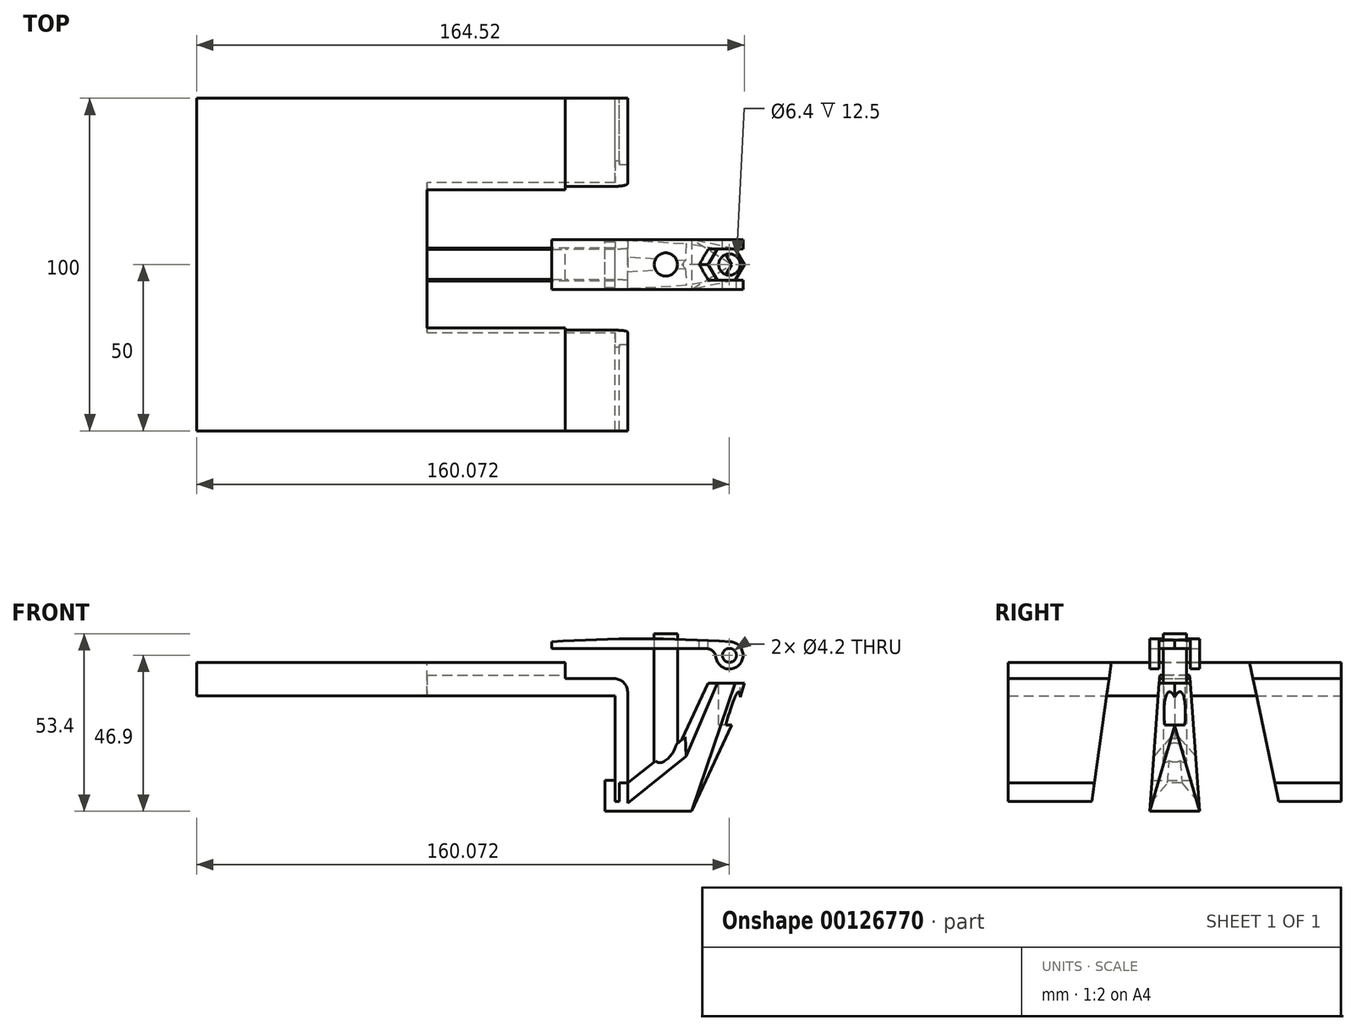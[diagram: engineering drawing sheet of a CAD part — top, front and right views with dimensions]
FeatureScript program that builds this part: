
annotation { "Feature Type Name" : "Feature", "Feature Type Description" : "" }
export const myFeature = defineFeature(function(context is Context, id is Id, definition is map)
    precondition{}
    {
        {
            var Q0;
            Q0=qCreatedBy(makeId("Front.planeOp"),FACE);
            var sketch = newSketch(context, id + "F0", { "sketchPlane" : qUnion([Q0])});
            skLineSegment(sketch, "E0", {"start": v(0, 36.9) * mm, "end": v(-18.75, 36.9) * mm});
            skLineSegment(sketch, "E1", {"start": v(-18.75, 36.9) * mm, "end": v(-18.75, 41.7) * mm});
            skLineSegment(sketch, "E2", {"start": v(-18.75, 41.7) * mm, "end": v(-129.48, 41.7) * mm});
            skLineSegment(sketch, "E3", {"start": v(-129.48, 41.7) * mm, "end": v(-129.48, 31.7) * mm});
            skLineSegment(sketch, "E4", {"start": v(-3.8, 0) * mm, "end": v(-2.5, 0) * mm});
            skLineSegment(sketch, "E5", {"start": v(-2.5, 0) * mm, "end": v(-2.5, 5.5) * mm});
            skLineSegment(sketch, "E6", {"start": v(-2.5, 5.5) * mm, "end": v(0, 5.5) * mm});
            skLineSegment(sketch, "E7", {"start": v(0, 5.5) * mm, "end": v(0, 36.9) * mm});
            skLineSegment(sketch, "E8", {"start": v(-3.8, 0) * mm, "end": v(-3.8, 31.7) * mm});
            skLineSegment(sketch, "E9", {"start": v(-3.8, 31.7) * mm, "end": v(-129.48, 31.7) * mm});
            skPoint(sketch, "E10.orphan", {"position": v(0, 0) * mm});
            skSolve(sketch);
        }
        {
            var Q0;
            Q0=makeQuery(id+"F0.imprint","IMPRINT",FACE,{"disambiguationData":[TD([[makeQuery(id+"F0.imprint","IMPRINT",EDGE,{"derivedFrom":sQuery(id+"F0.wireOp",EDGE,"E0")}),1.0]])]});
            extrude(context, id + "F1", {"entities" : qUnion([Q0]), "endBound" : BoundingType.SYMMETRIC, "depth" : 100 * mm});
        }
        {
            var Q0;
            Q0=makeQuery(id+"F1.opExtrude","SWEPT_EDGE",EDGE,{"disambiguationData":[OSD([sQuery(id+"F0.wireOp",EDGE,"E0"),sQuery(id+"F0.wireOp",EDGE,"E7")])]});
            fillet(context, id + "F2", {"entities" : qUnion([Q0]), "radius" : 4 * mm, "tangentPropagation" : true, "allowEdgeOverflow" : false});
        }
        {
            var Q0;
            Q0=qCreatedBy(makeId("Front.planeOp"),FACE);
            var sketch = newSketch(context, id + "F3", { "sketchPlane" : qUnion([Q0])});
            skLineSegment(sketch, "E11", {"start": v(-3.8, 6.32) * mm, "end": v(-3.8, 0) * mm});
            skLineSegment(sketch, "E12", {"start": v(-3.8, 0) * mm, "end": v(-2.5, 0) * mm});
            skLineSegment(sketch, "E13", {"start": v(-2.5, 0) * mm, "end": v(-2.5, 5.5) * mm});
            skLineSegment(sketch, "E14", {"start": v(-2.5, 5.5) * mm, "end": v(0, 5.5) * mm});
            skLineSegment(sketch, "E15", {"start": v(0, 5.5) * mm, "end": v(6.9, 5.5) * mm});
            skLineSegment(sketch, "E16", {"start": v(6.9, 5.5) * mm, "end": v(6.9, -3) * mm});
            skLineSegment(sketch, "E17", {"start": v(6.9, -3) * mm, "end": v(-6.8, -3) * mm});
            skLineSegment(sketch, "E18", {"start": v(-6.8, -3) * mm, "end": v(-6.8, 6.32) * mm});
            skLineSegment(sketch, "E19", {"start": v(-6.8, 6.32) * mm, "end": v(-3.8, 6.32) * mm});
            skSolve(sketch);
        }
        {
            var Q0;
            Q0=makeQuery(id+"F3.imprint","IMPRINT",FACE,{"disambiguationData":[TD([[makeQuery(id+"F3.imprint","IMPRINT",EDGE,{"derivedFrom":sQuery(id+"F3.wireOp",EDGE,"E11")}),-1.0]])]});
            extrude(context, id + "F4", {"entities" : qUnion([Q0]), "endBound" : BoundingType.SYMMETRIC, "depth" : 15 * mm});
        }
        {
            var Q0;
            Q0=makeQuery(id+"F4.opExtrude","SWEPT_FACE",FACE,{"disambiguationData":[OSD([sQuery(id+"F3.wireOp",EDGE,"E16")])]});
            extrude(context, id + "F5", {"entities" : qUnion([Q0]), "operationType" : NewBodyOperationType.ADD, "depth" : 3.69 * mm});
        }
        {
            var Q0;
            Q0=qCreatedBy(makeId("Top.planeOp"),FACE);
            cPlane(context, id + "F6", {"entities" : qUnion([Q0]), "cplaneType" : CPlaneType.OFFSET, "offset" : 38 * mm, "width" : 150 * mm, "height" : 150 * mm});
        }
        {
            var Q0;
            {var subQ0=sQuery(id+"F3.wireOp",EDGE,"E17");Q0=makeQuery(id+"F5.boolean.opBoolean","MERGE",FACE,{"derivedFrom":[makeQuery(id+"F4.opExtrude","SWEPT_FACE",FACE,{"disambiguationData":[OSD([subQ0])]}),makeQuery(id+"F5.opExtrude","SWEPT_FACE",FACE,{"disambiguationData":[OSD([sQuery(id+"F3.wireOp",EDGE,"E16"),subQ0])]})]});}
            var sketch = newSketch(context, id + "F7", { "sketchPlane" : qUnion([Q0])});
            skCircle(sketch, "E20.cCircle", {"center": v(14.92, 0) * mm, "radius": 7.5 * mm, "construction": true});
            skLineSegment(sketch, "E20.0", {"start": v(19.25, -7.5) * mm, "end": v(10.59, -7.5) * mm});
            skLineSegment(sketch, "E20.1", {"start": v(10.59, -7.5) * mm, "end": v(6.26, 0) * mm});
            skLineSegment(sketch, "E20.2", {"start": v(6.26, 0) * mm, "end": v(10.59, 7.5) * mm});
            skLineSegment(sketch, "E20.3", {"start": v(10.59, 7.5) * mm, "end": v(19.25, 7.5) * mm});
            skLineSegment(sketch, "E20.4", {"start": v(19.25, 7.5) * mm, "end": v(23.58, 0) * mm});
            skLineSegment(sketch, "E20.5", {"start": v(23.58, 0) * mm, "end": v(19.25, -7.5) * mm});
            skPoint(sketch, "E20.0.midPoint", {"position": v(14.92, -7.5) * mm});
            skSolve(sketch);
        }
        {
            var Q0;
            Q0=qCreatedBy(id+"F6.planeOp",FACE);
            var sketch = newSketch(context, id + "F8", { "sketchPlane" : qUnion([Q0])});
            skCircle(sketch, "E21.cCircle", {"center": v(30.6, 0) * mm, "radius": 4.5 * mm, "construction": true});
            skLineSegment(sketch, "E21.0", {"start": v(28, 4.5) * mm, "end": v(33.2, 4.5) * mm});
            skLineSegment(sketch, "E21.1", {"start": v(33.2, 4.5) * mm, "end": v(35.79, 0) * mm});
            skLineSegment(sketch, "E21.2", {"start": v(35.79, 0) * mm, "end": v(33.2, -4.5) * mm});
            skLineSegment(sketch, "E21.3", {"start": v(33.2, -4.5) * mm, "end": v(28, -4.5) * mm});
            skLineSegment(sketch, "E21.4", {"start": v(28, -4.5) * mm, "end": v(25.4, 0) * mm});
            skLineSegment(sketch, "E21.5", {"start": v(25.4, 0) * mm, "end": v(28, 4.5) * mm});
            skPoint(sketch, "E21.0.midPoint", {"position": v(30.6, 4.5) * mm});
            skSolve(sketch);
        }
        {
            var Q1;
            Q1=makeQuery(id+"F8.imprint","IMPRINT",FACE,{"disambiguationData":[TD([[makeQuery(id+"F8.imprint","IMPRINT",EDGE,{"derivedFrom":sQuery(id+"F8.wireOp",EDGE,"E21.0")}),-1.0]])]});
            var Q2;
            Q2 = qSketchRegion(id + "F7", true);
            loft(context, id + "F9", {"operationType" : NewBodyOperationType.ADD, "sheetProfilesArray" : [{ "sheetProfileEntities" : qUnion([Q1]) }, { "sheetProfileEntities" : qUnion([Q2]) }]});
        }
        {
            var Q0;
            {var subQ0=sQuery(id+"F3.wireOp",EDGE,"E16");Q0=makeQuery(id+"F5.boolean.opBoolean","MERGE",FACE,{"derivedFrom":[makeQuery(id+"F4.opExtrude","CAP_FACE",FACE,{"disambiguationData":[OSD([sQuery(id+"F3.wireOp",EDGE,"E11"),sQuery(id+"F3.wireOp",EDGE,"E12"),sQuery(id+"F3.wireOp",EDGE,"E13"),sQuery(id+"F3.wireOp",EDGE,"E14"),sQuery(id+"F3.wireOp",EDGE,"E15"),subQ0,sQuery(id+"F3.wireOp",EDGE,"E17"),sQuery(id+"F3.wireOp",EDGE,"E18"),sQuery(id+"F3.wireOp",EDGE,"E19")])],"isStart":false}),makeQuery(id+"F5.opExtrude","SWEPT_FACE",FACE,{"disambiguationData":[OSD([subQ0]),TDD([makeQuery(id+"F4.opExtrude","CAP_EDGE",EDGE,{"disambiguationData":[OSD([subQ0])],"isStart":false})])]})]});}
            var sketch = newSketch(context, id + "F10", { "sketchPlane" : qUnion([Q0])});
            skLineSegment(sketch, "E22", {"start": v(0, 5.5) * mm, "end": v(21.51, 22.74) * mm});
            skLineSegment(sketch, "E23", {"start": v(21.51, 22.74) * mm, "end": v(10.59, -3) * mm});
            skLineSegment(sketch, "E24", {"start": v(10.59, -3) * mm, "end": v(10.59, 5.5) * mm});
            skLineSegment(sketch, "E25", {"start": v(10.59, 5.5) * mm, "end": v(0, 5.5) * mm});
            skSolve(sketch);
        }
        {
            var Q0;
            Q0 = qSketchRegion(id + "F10", true);
            var Q1;
            {var subQ0=sQuery(id+"F3.wireOp",EDGE,"E16");Q1=makeQuery(id+"F5.boolean.opBoolean","MERGE",FACE,{"derivedFrom":[makeQuery(id+"F4.opExtrude","CAP_FACE",FACE,{"disambiguationData":[OSD([sQuery(id+"F3.wireOp",EDGE,"E11"),sQuery(id+"F3.wireOp",EDGE,"E12"),sQuery(id+"F3.wireOp",EDGE,"E13"),sQuery(id+"F3.wireOp",EDGE,"E14"),sQuery(id+"F3.wireOp",EDGE,"E15"),subQ0,sQuery(id+"F3.wireOp",EDGE,"E17"),sQuery(id+"F3.wireOp",EDGE,"E18"),sQuery(id+"F3.wireOp",EDGE,"E19")])],"isStart":true}),makeQuery(id+"F5.opExtrude","SWEPT_FACE",FACE,{"disambiguationData":[OSD([subQ0]),TDD([makeQuery(id+"F4.opExtrude","CAP_EDGE",EDGE,{"disambiguationData":[OSD([subQ0])],"isStart":true})])]})]});}
            extrude(context, id + "F11", {"entities" : qUnion([Q0]), "operationType" : NewBodyOperationType.ADD, "endBound" : BoundingType.UP_TO_SURFACE, "oppositeDirection" : true, "endBoundEntityFace" : qUnion([Q1]), "depth" : 25 * mm});
        }
        {
            var Q0;
            Q0=qCreatedBy(makeId("Right.planeOp"),FACE);
            var sketch = newSketch(context, id + "F12", { "sketchPlane" : qUnion([Q0])});
            skLineSegment(sketch, "E26.0", {"start": v(-4.5, 38) * mm, "end": v(-7.5, -3) * mm});
            skLineSegment(sketch, "E26.1", {"start": v(4.5, 38) * mm, "end": v(7.5, -3) * mm});
            skLineSegment(sketch, "E26.2", {"start": v(4.5, 38) * mm, "end": v(0, 38) * mm});
            skLineSegment(sketch, "E26.3", {"start": v(0, 38) * mm, "end": v(-4.5, 38) * mm});
            skLineSegment(sketch, "E27", {"start": v(-7.5, -3) * mm, "end": v(-25.27, -3) * mm});
            skLineSegment(sketch, "E28", {"start": v(-25.27, -3) * mm, "end": v(-18.5, 45.83) * mm});
            skLineSegment(sketch, "E29", {"start": v(-18.5, 45.83) * mm, "end": v(21.56, 46.28) * mm});
            skLineSegment(sketch, "E30", {"start": v(21.56, 46.28) * mm, "end": v(31.8, -3) * mm});
            skLineSegment(sketch, "E31", {"start": v(31.8, -3) * mm, "end": v(7.5, -3) * mm});
            skSolve(sketch);
        }
        {
            var Q0;
            Q0 = qSketchRegion(id + "F12", true);
            extrude(context, id + "F13", {"entities" : qUnion([Q0]), "operationType" : NewBodyOperationType.REMOVE, "endBound" : BoundingType.SYMMETRIC, "oppositeDirection" : true, "depth" : 120.63 * mm});
        }
        {
            var Q0;
            Q0=makeQuery(id+"F13.boolean.opBoolean","INTERSECT",EDGE,{"derivedFrom":[makeQuery(id+"F11.opExtrude","SWEPT_FACE",FACE,{"disambiguationData":[OSD([sQuery(id+"F10.wireOp",EDGE,"E22")])]}),makeQuery(id+"F13.opExtrude","SWEPT_FACE",FACE,{"disambiguationData":[OSD([sQuery(id+"F12.wireOp",EDGE,"E26.0")])]})]});
            var Q1;
            Q1=makeQuery(id+"F13.boolean.opBoolean","INTERSECT",EDGE,{"derivedFrom":[makeQuery(id+"F11.opExtrude","SWEPT_FACE",FACE,{"disambiguationData":[OSD([sQuery(id+"F10.wireOp",EDGE,"E22")])]}),makeQuery(id+"F13.opExtrude","SWEPT_FACE",FACE,{"disambiguationData":[OSD([sQuery(id+"F12.wireOp",EDGE,"E26.1")])]})]});
            chamfer(context, id + "F14", {"entities" : qUnion([Q0, Q1]), "width" : 5 * mm, "tangentPropagation" : true});
        }
        {
            var Q0;
            Q0=qCreatedBy(makeId("Front.planeOp"),FACE);
            var sketch = newSketch(context, id + "F15", { "sketchPlane" : qUnion([Q0])});
            skLineSegment(sketch, "E32", {"start": v(19.25, -3) * mm, "end": v(19.25, -3) * mm});
            skLineSegment(sketch, "E33", {"start": v(19.25, -3) * mm, "end": v(31.22, 22.66) * mm});
            skLineSegment(sketch, "E34", {"start": v(31.22, 22.66) * mm, "end": v(45.52, 4.83) * mm});
            skLineSegment(sketch, "E35", {"start": v(45.52, 4.83) * mm, "end": v(41.63, -16.09) * mm});
            skLineSegment(sketch, "E36", {"start": v(41.63, -16.09) * mm, "end": v(14.22, -13.6) * mm});
            skLineSegment(sketch, "E37", {"start": v(14.22, -13.6) * mm, "end": v(19.25, -3) * mm});
            skSolve(sketch);
        }
        {
            var Q0;
            Q0 = qSketchRegion(id + "F15", true);
            extrude(context, id + "F16", {"entities" : qUnion([Q0]), "operationType" : NewBodyOperationType.REMOVE, "endBound" : BoundingType.SYMMETRIC, "oppositeDirection" : true, "depth" : 25 * mm});
        }
        {
            var Q0;
            {var subQ0=sQuery(id+"F3.wireOp",EDGE,"E17");var subQ1=sQuery(id+"F3.wireOp",EDGE,"E16");Q0=makeQuery(id+"F9.boolean.opBoolean","MERGE",FACE,{"derivedFrom":[makeQuery(id+"F5.boolean.opBoolean","MERGE",FACE,{"derivedFrom":[makeQuery(id+"F4.opExtrude","SWEPT_FACE",FACE,{"disambiguationData":[OSD([subQ0])]}),makeQuery(id+"F5.opExtrude","SWEPT_FACE",FACE,{"disambiguationData":[OSD([subQ1,subQ0])]})]}),makeQuery(id+"F9.opLoft","CAP_FACE",FACE,{"disambiguationData":[OSD([makeQuery(id+"F7.imprint","IMPRINT",FACE,{"disambiguationData":[TD([[makeQuery(id+"F7.imprint","IMPRINT",EDGE,{"derivedFrom":sQuery(id+"F7.wireOp",EDGE,"E20.1")}),-1.0]])]})])],"isStart":true})]});}
            var sketch = newSketch(context, id + "F17", { "sketchPlane" : qUnion([Q0])});
            skCircle(sketch, "E38.cCircle", {"center": v(11.47, 0) * mm, "radius": 5.5 * mm, "construction": true});
            skLineSegment(sketch, "E38.0", {"start": v(8.3, 5.5) * mm, "end": v(14.65, 5.5) * mm});
            skLineSegment(sketch, "E38.1", {"start": v(14.65, 5.5) * mm, "end": v(17.82, 0) * mm});
            skLineSegment(sketch, "E38.2", {"start": v(17.82, 0) * mm, "end": v(14.65, -5.5) * mm});
            skLineSegment(sketch, "E38.3", {"start": v(14.65, -5.5) * mm, "end": v(8.3, -5.5) * mm});
            skLineSegment(sketch, "E38.4", {"start": v(8.3, -5.5) * mm, "end": v(5.12, 0) * mm});
            skLineSegment(sketch, "E38.5", {"start": v(5.12, 0) * mm, "end": v(8.3, 5.5) * mm});
            skPoint(sketch, "E38.0.midPoint", {"position": v(11.47, 5.5) * mm});
            skSolve(sketch);
        }
        {
            var Q0;
            Q0 = qSketchRegion(id + "F17", true);
            extrude(context, id + "F18", {"entities" : qUnion([Q0]), "operationType" : NewBodyOperationType.REMOVE, "oppositeDirection" : true, "depth" : 5 * mm});
        }
        {
            var Q0;
            Q0=makeQuery(id+"F18.boolean.opBoolean","COPY",FACE,{"derivedFrom":makeQuery(id+"F18.opExtrude","CAP_FACE",FACE,{"disambiguationData":[OSD([sQuery(id+"F17.wireOp",EDGE,"E38.0"),sQuery(id+"F17.wireOp",EDGE,"E38.1"),sQuery(id+"F17.wireOp",EDGE,"E38.2"),sQuery(id+"F17.wireOp",EDGE,"E38.3"),sQuery(id+"F17.wireOp",EDGE,"E38.4"),sQuery(id+"F17.wireOp",EDGE,"E38.5")])],"isStart":false})});
            var sketch = newSketch(context, id + "F19", { "sketchPlane" : qUnion([Q0])});
            skCircle(sketch, "E39", {"center": v(11.47, 0) * mm, "radius": 3.5 * mm});
            skSolve(sketch);
        }
        {
            var Q0;
            Q0 = qSketchRegion(id + "F19", true);
            extrude(context, id + "F20", {"entities" : qUnion([Q0]), "operationType" : NewBodyOperationType.REMOVE, "endBound" : BoundingType.THROUGH_ALL, "oppositeDirection" : true, "depth" : 25 * mm});
        }
        {
            var Q0;
            Q0=makeQuery(id+"F18.boolean.opBoolean","COPY",FACE,{"derivedFrom":makeQuery(id+"F18.opExtrude","CAP_FACE",FACE,{"disambiguationData":[OSD([sQuery(id+"F17.wireOp",EDGE,"E38.0"),sQuery(id+"F17.wireOp",EDGE,"E38.1"),sQuery(id+"F17.wireOp",EDGE,"E38.2"),sQuery(id+"F17.wireOp",EDGE,"E38.3"),sQuery(id+"F17.wireOp",EDGE,"E38.4"),sQuery(id+"F17.wireOp",EDGE,"E38.5")])],"isStart":false})});
            var Q1;
            {var subQ0=sQuery(id+"F3.wireOp",EDGE,"E17");var subQ1=sQuery(id+"F3.wireOp",EDGE,"E16");Q1=makeQuery(id+"F9.boolean.opBoolean","MERGE",FACE,{"derivedFrom":[makeQuery(id+"F5.boolean.opBoolean","MERGE",FACE,{"derivedFrom":[makeQuery(id+"F4.opExtrude","SWEPT_FACE",FACE,{"disambiguationData":[OSD([subQ0])]}),makeQuery(id+"F5.opExtrude","SWEPT_FACE",FACE,{"disambiguationData":[OSD([subQ1,subQ0])]})]}),makeQuery(id+"F9.opLoft","CAP_FACE",FACE,{"disambiguationData":[OSD([makeQuery(id+"F7.imprint","IMPRINT",FACE,{"disambiguationData":[TD([[makeQuery(id+"F7.imprint","IMPRINT",EDGE,{"derivedFrom":sQuery(id+"F7.wireOp",EDGE,"E20.1")}),-1.0]])]})])],"isStart":true})]});}
            extrude(context, id + "F21", {"entities" : qUnion([Q0]), "endBound" : BoundingType.UP_TO_SURFACE, "endBoundEntityFace" : qUnion([Q1]), "depth" : 25 * mm});
        }
        {
            var Q0;
            Q0=makeQuery(id+"F21.opExtrude","CAP_FACE",FACE,{"disambiguationData":[OSD([sQuery(id+"F17.wireOp",EDGE,"E38.0"),sQuery(id+"F17.wireOp",EDGE,"E38.1"),sQuery(id+"F17.wireOp",EDGE,"E38.2"),sQuery(id+"F17.wireOp",EDGE,"E38.3"),sQuery(id+"F17.wireOp",EDGE,"E38.4"),sQuery(id+"F17.wireOp",EDGE,"E38.5")])],"isStart":false});
            var sketch = newSketch(context, id + "F22", { "sketchPlane" : qUnion([Q0])});
            skCircle(sketch, "E40", {"center": v(11.47, 0) * mm, "radius": 3.5 * mm});
            skSolve(sketch);
        }
        {
            var Q0;
            Q0 = qSketchRegion(id + "F22", true);
            extrude(context, id + "F23", {"entities" : qUnion([Q0]), "operationType" : NewBodyOperationType.ADD, "oppositeDirection" : true, "depth" : 53.4 * mm});
        }
        {
            var Q0;
            Q0=makeQuery(id+"F9.opLoft","CAP_FACE",FACE,{"disambiguationData":[OSD([makeQuery(id+"F8.imprint","IMPRINT",FACE,{"disambiguationData":[TD([[makeQuery(id+"F8.imprint","IMPRINT",EDGE,{"derivedFrom":sQuery(id+"F8.wireOp",EDGE,"E21.0")}),-1.0]])]})])],"isStart":true});
            var sketch = newSketch(context, id + "F24", { "sketchPlane" : qUnion([Q0])});
            skCircle(sketch, "E41", {"center": v(30.6, 0) * mm, "radius": 3 * mm});
            skLineSegment(sketch, "E42", {"start": v(28, 4.5) * mm, "end": v(33.2, -4.5) * mm, "construction": true});
            skLineSegment(sketch, "E43", {"start": v(28, -4.5) * mm, "end": v(33.2, 4.5) * mm, "construction": true});
            skSolve(sketch);
        }
        {
            var Q0;
            Q0 = qSketchRegion(id + "F24", true);
            extrude(context, id + "F25", {"entities" : qUnion([Q0]), "operationType" : NewBodyOperationType.ADD, "depth" : 8 * mm});
        }
        {
            var Q0;
            Q0=makeQuery(id+"F9.opLoft","CAP_FACE",FACE,{"disambiguationData":[OSD([makeQuery(id+"F8.imprint","IMPRINT",FACE,{"disambiguationData":[TD([[makeQuery(id+"F8.imprint","IMPRINT",EDGE,{"derivedFrom":sQuery(id+"F8.wireOp",EDGE,"E21.0")}),-1.0]])]})])],"isStart":true});
            extrude(context, id + "F26", {"entities" : qUnion([Q0]), "depth" : 10 * mm});
        }
        {
            var Q0;
            Q0=qCreatedBy(makeId("Front.planeOp"),FACE);
            var sketch = newSketch(context, id + "F27", { "sketchPlane" : qUnion([Q0])});
            skCircle(sketch, "E44", {"center": v(30.6, 43.9) * mm, "radius": 2.1 * mm});
            skLineSegment(sketch, "E45", {"start": v(30.6, 48) * mm, "end": v(30.6, 37.26) * mm, "construction": true});
            skSolve(sketch);
        }
        {
            var Q0;
            Q0 = qSketchRegion(id + "F27", true);
            extrude(context, id + "F28", {"entities" : qUnion([Q0]), "operationType" : NewBodyOperationType.ADD, "endBound" : BoundingType.SYMMETRIC, "depth" : 15 * mm});
        }
        {
            var Q0;
            Q0=makeQuery(id+"F26.opExtrude","CAP_FACE",FACE,{"disambiguationData":[OSD([makeQuery(id+"F8.imprint","IMPRINT",FACE,{"disambiguationData":[TD([[makeQuery(id+"F8.imprint","IMPRINT",EDGE,{"derivedFrom":sQuery(id+"F8.wireOp",EDGE,"E21.0")}),-1.0]])]})])],"isStart":false});
            var sketch = newSketch(context, id + "F29", { "sketchPlane" : qUnion([Q0])});
            skCircle(sketch, "E46", {"center": v(30.6, 0) * mm, "radius": 3.2 * mm});
            skSolve(sketch);
        }
        {
            var Q0;
            Q0 = qSketchRegion(id + "F29", true);
            extrude(context, id + "F30", {"entities" : qUnion([Q0]), "operationType" : NewBodyOperationType.REMOVE, "oppositeDirection" : true, "depth" : 25 * mm});
        }
        {
            var Q0;
            Q0=qCreatedBy(makeId("Front.planeOp"),FACE);
            var sketch = newSketch(context, id + "F31", { "sketchPlane" : qUnion([Q0])});
            skCircle(sketch, "E47.0", {"center": v(30.6, 43.9) * mm, "radius": 2.1 * mm});
            skCircle(sketch, "E48", {"center": v(30.6, 43.9) * mm, "radius": 4.1 * mm});
            skArc(sketch, "E49", {"start": v(30.86, 48) * mm, "mid": v(4.06, 48.88) * mm, "end": v(-22.75, 48) * mm});
            skLineSegment(sketch, "E50", {"start": v(-22.75, 48) * mm, "end": v(-22.75, 46) * mm});
            skLineSegment(sketch, "E51", {"start": v(-22.75, 46) * mm, "end": v(23.55, 46) * mm});
            skArc(sketch, "E52", {"start": v(26.53, 43.38) * mm, "mid": v(25.53, 45.24) * mm, "end": v(23.55, 46) * mm});
            skSolve(sketch);
        }
        {
            var Q0;
            Q0 = qSketchRegion(id + "F31", true);
            extrude(context, id + "F32", {"entities" : qUnion([Q0]), "endBound" : BoundingType.SYMMETRIC, "depth" : 15 * mm});
        }
        {
            var Q0;
            Q0=makeQuery(id+"F26.opExtrude","CAP_FACE",FACE,{"disambiguationData":[OSD([makeQuery(id+"F8.imprint","IMPRINT",FACE,{"disambiguationData":[TD([[makeQuery(id+"F8.imprint","IMPRINT",EDGE,{"derivedFrom":sQuery(id+"F8.wireOp",EDGE,"E21.0")}),-1.0]])]})])],"isStart":false});
            var sketch = newSketch(context, id + "F33", { "sketchPlane" : qUnion([Q0])});
            skCircle(sketch, "E53.cCircle", {"center": v(26.96, 0) * mm, "radius": 4.7 * mm, "construction": true});
            skLineSegment(sketch, "E53.0", {"start": v(24.24, 4.7) * mm, "end": v(29.67, 4.7) * mm});
            skLineSegment(sketch, "E53.3", {"start": v(29.67, -4.7) * mm, "end": v(24.24, -4.7) * mm});
            skLineSegment(sketch, "E53.4", {"start": v(24.24, -4.7) * mm, "end": v(21.53, 0) * mm});
            skLineSegment(sketch, "E53.5", {"start": v(21.53, 0) * mm, "end": v(24.24, 4.7) * mm});
            skPoint(sketch, "E53.0.midPoint", {"position": v(26.96, 4.7) * mm});
            skLineSegment(sketch, "E54.bottom", {"start": v(29.67, 4.7) * mm, "end": v(49.23, 4.7) * mm});
            skLineSegment(sketch, "E54.top", {"start": v(29.67, -4.7) * mm, "end": v(49.23, -4.7) * mm});
            skLineSegment(sketch, "E54.right", {"start": v(49.23, 4.7) * mm, "end": v(49.23, -4.7) * mm});
            skPoint(sketch, "E54.middle", {"position": v(39.45, 0) * mm});
            skPoint(sketch, "E55.orphan", {"position": v(32.38, 0) * mm});
            skSolve(sketch);
        }
        {
            var Q0;
            Q0 = qSketchRegion(id + "F33", true);
            extrude(context, id + "F34", {"entities" : qUnion([Q0]), "operationType" : NewBodyOperationType.REMOVE, "endBound" : BoundingType.SYMMETRIC, "oppositeDirection" : true, "depth" : 25 * mm});
        }
    });
